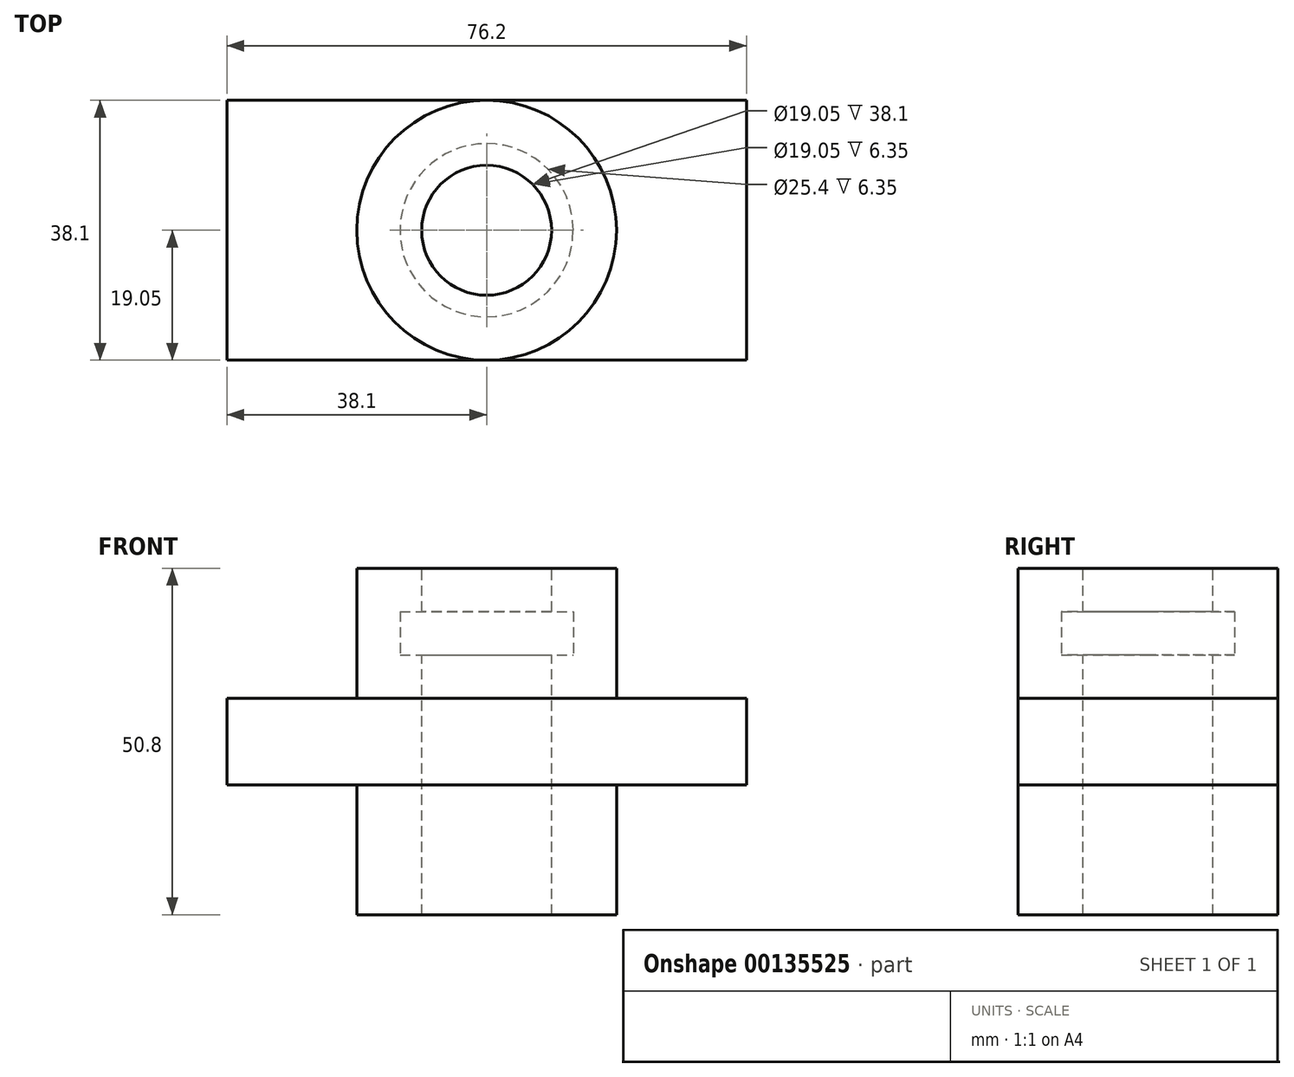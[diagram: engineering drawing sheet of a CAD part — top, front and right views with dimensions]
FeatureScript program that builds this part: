
annotation { "Feature Type Name" : "Feature", "Feature Type Description" : "" }
export const myFeature = defineFeature(function(context is Context, id is Id, definition is map)
    precondition{}
    {
        {
            var Q0;
            Q0=qCreatedBy(makeId("Top.planeOp"),FACE);
            var sketch = newSketch(context, id + "F0", { "sketchPlane" : qUnion([Q0])});
            skCircle(sketch, "E0", {"center": v(0, 0) * mm, "radius": 19.05 * mm});
            skCircle(sketch, "E1", {"center": v(0, 0) * mm, "radius": 9.53 * mm});
            skCircle(sketch, "E2", {"center": v(0, 0) * mm, "radius": 12.7 * mm, "construction": true});
            skLineSegment(sketch, "E3.bottom", {"start": v(38.1, 19.05) * mm, "end": v(-38.1, 19.05) * mm});
            skLineSegment(sketch, "E3.top", {"start": v(38.1, -19.05) * mm, "end": v(-38.1, -19.05) * mm});
            skLineSegment(sketch, "E3.left", {"start": v(38.1, 19.05) * mm, "end": v(38.1, -19.05) * mm});
            skLineSegment(sketch, "E3.right", {"start": v(-38.1, 19.05) * mm, "end": v(-38.1, -19.05) * mm});
            skSolve(sketch);
        }
        {
            var Q0;
            {var subQ0=sQuery(id+"F0.wireOp",EDGE,"BSl3NDpU-5uvg-v05H-KPbn-8CthVEBvHAjv");Q0=makeQuery(id+"F0.imprint","IMPRINT",FACE,{"disambiguationData":[TD([[makeQuery(id+"F0.imprint","IMPRINT",EDGE,{"derivedFrom":subQ0}),-1.0]])]});}
            var Q1;
            Q1=makeQuery(id+"F0.imprint","IMPRINT",FACE,{"disambiguationData":[TD([[makeQuery(id+"F0.imprint","IMPRINT",EDGE,{"derivedFrom":sQuery(id+"F0.wireOp",EDGE,"E1")}),-1.0]])]});
            var Q2;
            {var subQ0=sQuery(id+"F0.wireOp",EDGE,"YbOceSSM-IHOE-DUEN-b6yr-6a2GgnUvuhXw");Q2=makeQuery(id+"F0.imprint","IMPRINT",FACE,{"disambiguationData":[TD([[makeQuery(id+"F0.imprint","IMPRINT",EDGE,{"derivedFrom":subQ0}),-1.0]])]});}
            var Q3;
            {var subQ5=sQuery(id+"F0.wireOp",EDGE,"E3.right");Q3=makeQuery(id+"F0.imprint","IMPRINT",FACE,{"disambiguationData":[TD([[makeQuery(id+"F0.imprint","IMPRINT",EDGE,{"derivedFrom":subQ5}),1.0]])]});}
            var Q4;
            {var subQ5=sQuery(id+"F0.wireOp",EDGE,"E3.left");Q4=makeQuery(id+"F0.imprint","IMPRINT",FACE,{"disambiguationData":[TD([[makeQuery(id+"F0.imprint","IMPRINT",EDGE,{"derivedFrom":subQ5}),-1.0]])]});}
            extrude(context, id + "F1", {"entities" : qUnion([Q0, Q1, Q2, Q3, Q4]), "oppositeDirection" : true, "depth" : 12.7 * mm});
        }
        {
            var Q0;
            Q0=makeQuery(id+"F0.imprint","IMPRINT",FACE,{"disambiguationData":[TD([[makeQuery(id+"F0.imprint","IMPRINT",EDGE,{"derivedFrom":sQuery(id+"F0.wireOp",EDGE,"E1")}),-1.0]])]});
            extrude(context, id + "F2", {"entities" : qUnion([Q0]), "operationType" : NewBodyOperationType.ADD, "depth" : 19.05 * mm, "hasSecondDirection" : true, "secondDirectionOppositeDirection" : true, "secondDirectionDepth" : 31.75 * mm});
        }
        {
            var Q0;
            Q0=qCreatedBy(makeId("Right.planeOp"),FACE);
            var sketch = newSketch(context, id + "F3", { "sketchPlane" : qUnion([Q0])});
            skLineSegment(sketch, "E4", {"start": v(0, 19.05) * mm, "end": v(0, -31.75) * mm, "construction": true});
            skLineSegment(sketch, "E5", {"start": v(0, -31.75) * mm, "end": v(12.7, -31.75) * mm, "construction": true});
            skLineSegment(sketch, "E6", {"start": v(12.7, -31.75) * mm, "end": v(12.7, 0) * mm, "construction": true});
            skLineSegment(sketch, "E7", {"start": v(12.7, 0) * mm, "end": v(12.7, 19.05) * mm, "construction": true});
            skLineSegment(sketch, "E8", {"start": v(12.7, 19.05) * mm, "end": v(0, 19.05) * mm, "construction": true});
            skLineSegment(sketch, "E9", {"start": v(0, 6.35) * mm, "end": v(12.7, 6.35) * mm});
            skLineSegment(sketch, "E10", {"start": v(12.7, 6.35) * mm, "end": v(12.7, 12.7) * mm});
            skLineSegment(sketch, "E11", {"start": v(12.7, 12.7) * mm, "end": v(0, 12.7) * mm});
            skLineSegment(sketch, "E12", {"start": v(0, 12.7) * mm, "end": v(0, 6.35) * mm});
            skSolve(sketch);
        }
        {
            var Q0;
            Q0 = qSketchRegion(id + "F3", true);
            var Q1;
            Q1=sQuery(id+"F3.wireOp",EDGE,"E4");
            revolve(context, id + "F4", {"operationType" : NewBodyOperationType.REMOVE, "entities" : qUnion([Q0]), "axis" : qUnion([Q1]), "revolveType" : RevolveType.FULL, "oppositeDirection" : true});
        }
    });
